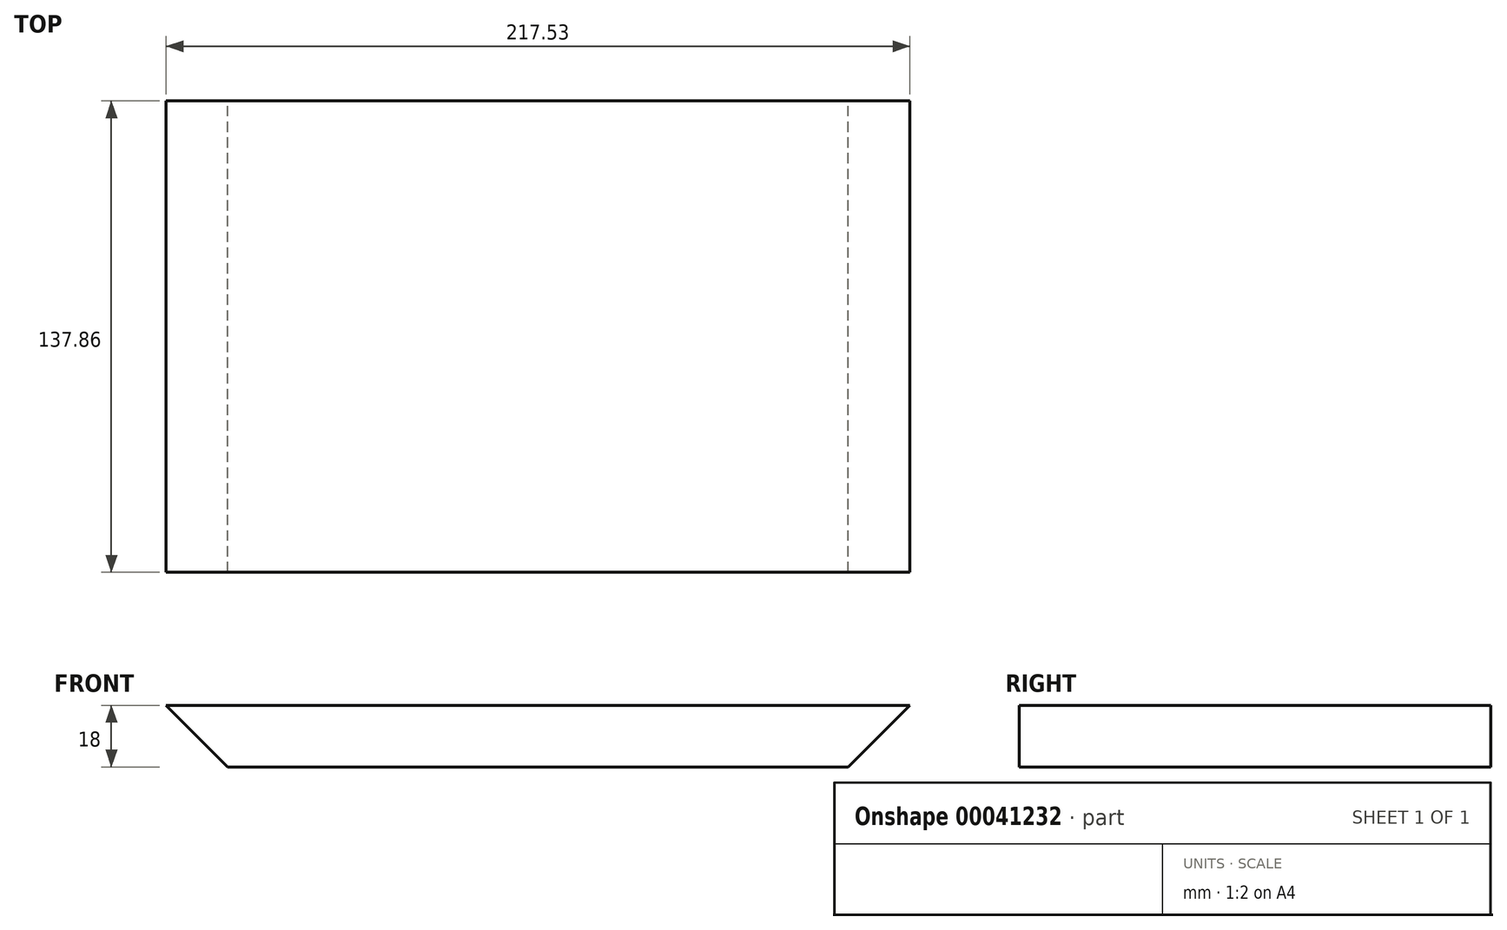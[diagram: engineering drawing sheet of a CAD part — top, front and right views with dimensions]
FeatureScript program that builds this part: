
annotation { "Feature Type Name" : "Feature", "Feature Type Description" : "" }
export const myFeature = defineFeature(function(context is Context, id is Id, definition is map)
    precondition{}
    {
        {
            var Q0;
            Q0=qCreatedBy(makeId("Front.planeOp"),FACE);
            var sketch = newSketch(context, id + "F0", { "sketchPlane" : qUnion([Q0])});
            skLineSegment(sketch, "E0.bottom", {"start": v(-107.34, -6.95) * mm, "end": v(110.2, -6.95) * mm});
            skLineSegment(sketch, "E0.top", {"start": v(-89.34, -24.95) * mm, "end": v(92.2, -24.95) * mm});
            skLineSegment(sketch, "E1", {"start": v(-107.34, -6.95) * mm, "end": v(-89.34, -24.95) * mm});
            skLineSegment(sketch, "E2", {"start": v(110.2, -6.95) * mm, "end": v(92.2, -24.95) * mm});
            skSolve(sketch);
        }
        {
            var Q0;
            Q0 = qSketchRegion(id + "F0", true);
            extrude(context, id + "F1", {"entities" : qUnion([Q0]), "depth" : 149.86 * mm - 12 * mm});
        }
    });
